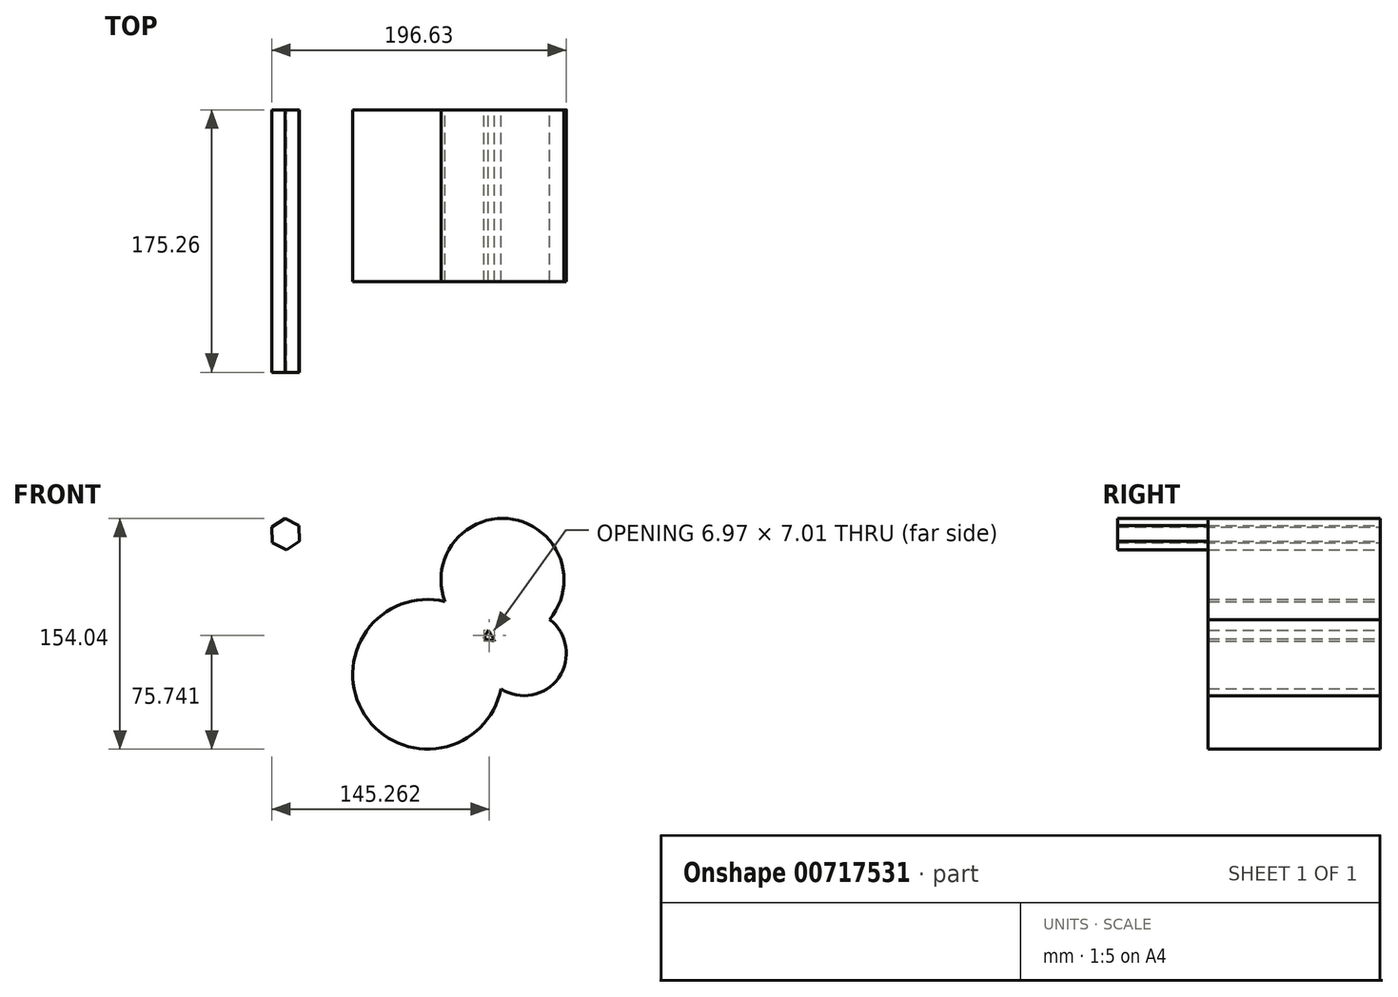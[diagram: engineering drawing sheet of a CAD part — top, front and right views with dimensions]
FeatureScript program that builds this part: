
annotation { "Feature Type Name" : "Feature", "Feature Type Description" : "" }
export const myFeature = defineFeature(function(context is Context, id is Id, definition is map)
    precondition{}
    {
        {
            var Q0;
            Q0=qCreatedBy(makeId("Front.planeOp"),FACE);
            var sketch = newSketch(context, id + "F0", { "sketchPlane" : qUnion([Q0])});
            skCircle(sketch, "E0", {"center": v(-5.77, 18.95) * mm, "radius": 41.07 * mm});
            skCircle(sketch, "E1", {"center": v(8.56, -30.03) * mm, "radius": 28.3 * mm});
            skCircle(sketch, "E2", {"center": v(-55.74, -44.05) * mm, "radius": 49.96 * mm});
            skSolve(sketch);
        }
        {
            var Q0;
            Q0 = qSketchRegion(id + "F0", true);
            extrude(context, id + "F1", {"entities" : qUnion([Q0]), "depth" : 114.8 * mm, "offsetDistance" : 25.4 * mm});
        }
        {
            var Q0;
            Q0=qCreatedBy(makeId("Front.planeOp"),FACE);
            var sketch = newSketch(context, id + "F2", { "sketchPlane" : qUnion([Q0])});
            skCircle(sketch, "E3.cCircle", {"center": v(-150.45, 49.53) * mm, "radius": 9.1 * mm, "construction": true});
            skLineSegment(sketch, "E3.0", {"start": v(-141.13, 44.68) * mm, "end": v(-149.99, 39.03) * mm});
            skLineSegment(sketch, "E3.1", {"start": v(-149.99, 39.03) * mm, "end": v(-159.31, 43.88) * mm});
            skLineSegment(sketch, "E3.2", {"start": v(-159.31, 43.88) * mm, "end": v(-159.77, 54.38) * mm});
            skLineSegment(sketch, "E3.3", {"start": v(-159.77, 54.38) * mm, "end": v(-150.91, 60.03) * mm});
            skLineSegment(sketch, "E3.4", {"start": v(-150.91, 60.03) * mm, "end": v(-141.59, 55.18) * mm});
            skLineSegment(sketch, "E3.5", {"start": v(-141.59, 55.18) * mm, "end": v(-141.13, 44.68) * mm});
            skPoint(sketch, "E3.0.midPoint", {"position": v(-145.56, 41.86) * mm});
            skSolve(sketch);
        }
        {
            var Q0;
            Q0 = qSketchRegion(id + "F2", true);
            extrude(context, id + "F3", {"entities" : qUnion([Q0]), "depth" : 175.26 * mm, "offsetDistance" : 25.4 * mm});
        }
    });
